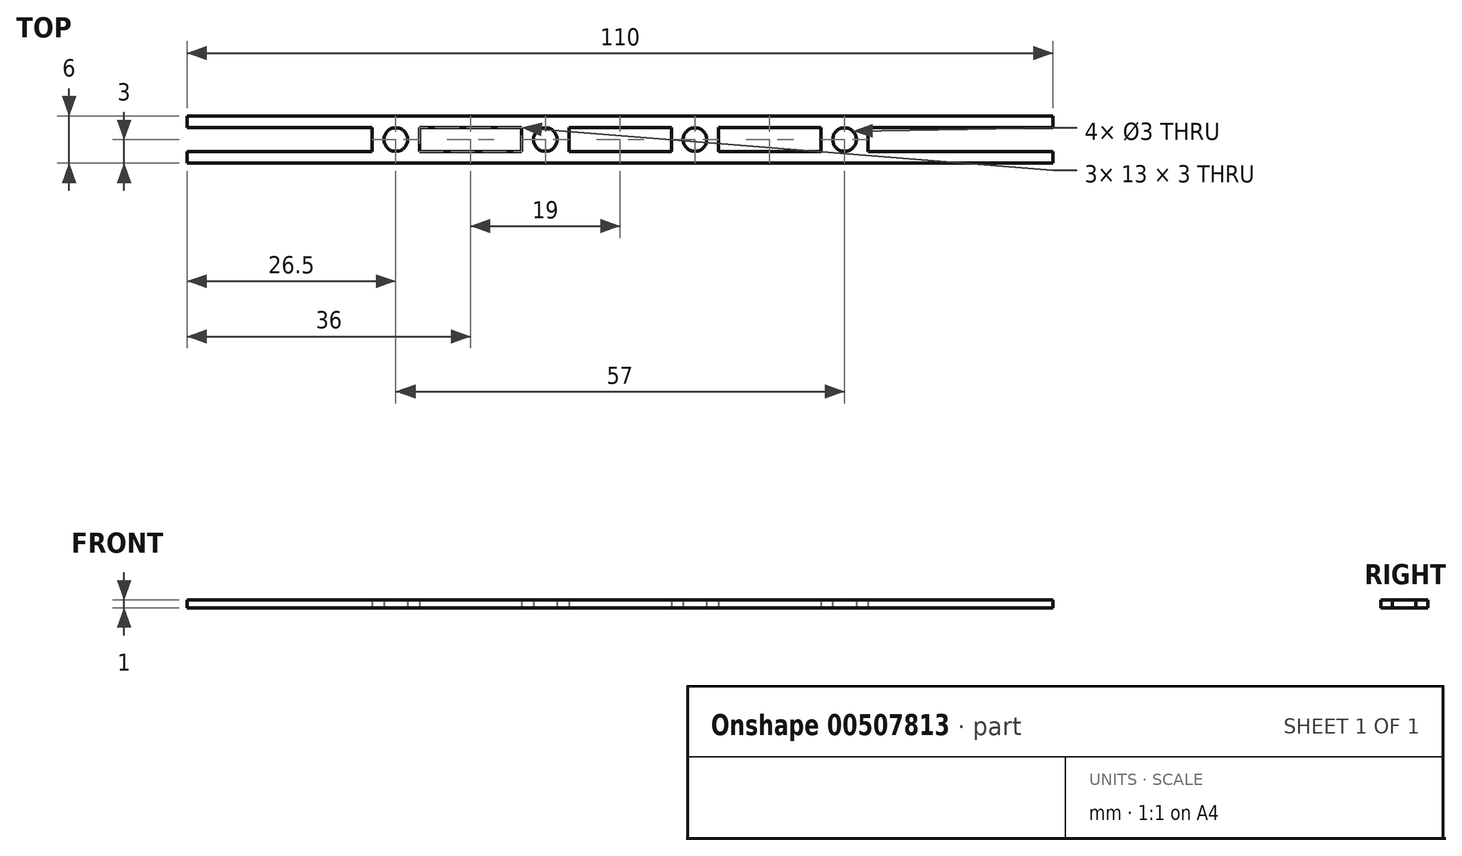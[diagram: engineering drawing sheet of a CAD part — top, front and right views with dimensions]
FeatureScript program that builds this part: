
annotation { "Feature Type Name" : "Feature", "Feature Type Description" : "" }
export const myFeature = defineFeature(function(context is Context, id is Id, definition is map)
    precondition{}
    {
        {
            var Q0;
            Q0=qCreatedBy(makeId("Top.planeOp"),FACE);
            var sketch = newSketch(context, id + "F0", { "sketchPlane" : qUnion([Q0])});
            skLineSegment(sketch, "E0.bottom", {"start": v(0, 3) * mm, "end": v(-55, 3) * mm});
            skLineSegment(sketch, "E0.top", {"start": v(0, -3) * mm, "end": v(-55, -3) * mm});
            skLineSegment(sketch, "E0.left", {"start": v(0, 3) * mm, "end": v(0, -3) * mm});
            skLineSegment(sketch, "E0.right", {"start": v(-55, 3) * mm, "end": v(-55, -3) * mm});
            skCircle(sketch, "E1", {"center": v(-9.5, 0) * mm, "radius": 1.5 * mm});
            skCircle(sketch, "E2", {"center": v(-28.5, 0) * mm, "radius": 1.5 * mm});
            skLineSegment(sketch, "E3.bottom", {"start": v(-55, 1.5) * mm, "end": v(-31.5, 1.5) * mm});
            skLineSegment(sketch, "E3.top", {"start": v(-55, -1.5) * mm, "end": v(-31.5, -1.5) * mm});
            skLineSegment(sketch, "E3.left", {"start": v(-55, 1.5) * mm, "end": v(-55, -1.5) * mm});
            skLineSegment(sketch, "E3.right", {"start": v(-31.5, 1.5) * mm, "end": v(-31.5, -1.5) * mm});
            skPoint(sketch, "E3.middle", {"position": v(-43.25, 0) * mm});
            skLineSegment(sketch, "E4.bottom", {"start": v(-12.5, 1.5) * mm, "end": v(-25.5, 1.5) * mm});
            skLineSegment(sketch, "E4.top", {"start": v(-12.5, -1.5) * mm, "end": v(-25.5, -1.5) * mm});
            skLineSegment(sketch, "E4.left", {"start": v(-12.5, 1.5) * mm, "end": v(-12.5, -1.5) * mm});
            skLineSegment(sketch, "E4.right", {"start": v(-25.5, 1.5) * mm, "end": v(-25.5, -1.5) * mm});
            skPoint(sketch, "E4.middle", {"position": v(-19, 0) * mm});
            skLineSegment(sketch, "E5.bottom", {"start": v(0, -1.5) * mm, "end": v(-6.5, -1.5) * mm});
            skLineSegment(sketch, "E5.top", {"start": v(0, 1.5) * mm, "end": v(-6.5, 1.5) * mm});
            skLineSegment(sketch, "E5.left", {"start": v(0, -1.5) * mm, "end": v(0, 1.5) * mm});
            skLineSegment(sketch, "E5.right", {"start": v(-6.5, -1.5) * mm, "end": v(-6.5, 1.5) * mm});
            skLineSegment(sketch, "E6.MirrorCS", {"start": v(55, 3) * mm, "end": v(55, -3) * mm});
            skPoint(sketch, "E7.MirrorP", {"position": v(19, 0) * mm});
            skLineSegment(sketch, "E8.MirrorCS", {"start": v(6.5, -1.5) * mm, "end": v(6.5, 1.5) * mm});
            skLineSegment(sketch, "E9.MirrorCS", {"start": v(25.5, 1.5) * mm, "end": v(25.5, -1.5) * mm});
            skLineSegment(sketch, "E10.MirrorCS", {"start": v(0, -3) * mm, "end": v(55, -3) * mm});
            skLineSegment(sketch, "E11.MirrorCS", {"start": v(0, 3) * mm, "end": v(55, 3) * mm});
            skLineSegment(sketch, "E12.MirrorCS", {"start": v(12.5, 1.5) * mm, "end": v(12.5, -1.5) * mm});
            skLineSegment(sketch, "E13.MirrorCS", {"start": v(12.5, -1.5) * mm, "end": v(25.5, -1.5) * mm});
            skLineSegment(sketch, "E14.MirrorCS", {"start": v(0, -1.5) * mm, "end": v(6.5, -1.5) * mm});
            skPoint(sketch, "E15.MirrorP", {"position": v(43.25, 0) * mm});
            skCircle(sketch, "E16.MirrorC", {"center": v(9.5, 0) * mm, "radius": 1.5 * mm});
            skLineSegment(sketch, "E17.MirrorCS", {"start": v(12.5, 1.5) * mm, "end": v(25.5, 1.5) * mm});
            skLineSegment(sketch, "E18.MirrorCS", {"start": v(55, 1.5) * mm, "end": v(31.5, 1.5) * mm});
            skCircle(sketch, "E19.MirrorC", {"center": v(28.5, 0) * mm, "radius": 1.5 * mm});
            skLineSegment(sketch, "E20.MirrorCS", {"start": v(55, -1.5) * mm, "end": v(31.5, -1.5) * mm});
            skLineSegment(sketch, "E21.MirrorCS", {"start": v(0, 1.5) * mm, "end": v(6.5, 1.5) * mm});
            skLineSegment(sketch, "E22.MirrorCS", {"start": v(55, 1.5) * mm, "end": v(55, -1.5) * mm});
            skLineSegment(sketch, "E23.MirrorCS", {"start": v(31.5, 1.5) * mm, "end": v(31.5, -1.5) * mm});
            skSolve(sketch);
        }
        {
            var Q0;
            {var subQ2=sQuery(id+"F0.wireOp",EDGE,"E0.bottom");Q0=makeQuery(id+"F0.imprint","IMPRINT",FACE,{"disambiguationData":[TD([[makeQuery(id+"F0.imprint","IMPRINT",EDGE,{"derivedFrom":subQ2}),1.0]])]});}
            var Q1;
            Q1=makeQuery(id+"F0.imprint","IMPRINT",FACE,{"disambiguationData":[TD([[makeQuery(id+"F0.imprint","IMPRINT",EDGE,{"derivedFrom":sQuery(id+"F0.wireOp",EDGE,"E8.MirrorCS")}),-1.0]])]});
            extrude(context, id + "F1", {"entities" : qUnion([Q0, Q1]), "depth" : 1 * mm});
        }
    });
